# Revit family: IS_iLifeB_T5344_BIM_GB
name_source: partatom
category: Plumbing Fixtures
units: mm (PartAtom-declared; Revit-internal decimal feet)

## family parameters
Always vertical = No
Cut with Voids When Loaded = No
OmniClass Number = 23.45.05.14.14
OmniClass Title = Sinks/Lavatories
Part Type = Normal
Room Calculation Point = No
Round Connector Dimension = Use Diameter
Shared = No
Work Plane-Based = No

## types (2) — shared parameters
BIMobject category = Wash Basins
BIMobject category code = wash-basins
BIMobject main category = Sanitary
BIMobject main category code = sanitary
Brand url = http://www.idealstandard.co.uk
Date of publishing = 22/07/2022
Edition number = 1
GTIN code = https://8014140503873
IFC Classification = Sanitary Terminal
Installation instructions = https://www.idealstandard.co.uk
Manufacturer = Ideal Standard
Manufacturer name = Ideal Standard
Material main = Fireclay
NBS Reference Code = 45-35-70/368
NBS Reference Description = Wall hung hand rinse basins
NominalDepth = 440 mm
NominalHeight = 180 mm
NominalWidth = 549 mm
OmniClass Code = 23-39 29 13 21 19
OmniClass Description = Surface Water Retention Basins
Product Guid = 4836061b-5428-4228-a0b7-367d902eb1b3
Product SKU = T5344
Product certification = https://www.idealstandard.co.uk
Product data url = https://bimobject.com
Product family = Washbasin
Product group = Sanitary
Product name = I.Life b basin 55 cm with center taphole
Product url = https://www.idealstandard.co.uk
QR code = http://bimobject.com
Size = 550 x 440 x 180 mm
Technical description = https://www.idealstandard.co.uk
UNSPSC Code = 301815
URL = https://www.idealstandard.co.uk
Uniclass 2015 Code = Pr_40_20_96_96
Uniclass 2015 Name = Wall-hung washbasins
Youtube clip = https://www.youtube.com

## per-type parameters (varying)
| type | Description | Model |
| T534401 - Ideal Standard i.life B  basin 55 cm with center taphole and without overflow - White Finish | Ideal Standard i.life B  basin 55 cm with center taphole, without overflow, white, in carton box, EU pallet | T534401 |
| T5344MA - Ideal Standard i.life B  basin 55 cm with center taphole and without overflow  - Ideal Plus White | Ideal Standard i.life B  basin 55 cm with center taphole, without overflow, white Ideal Plus, in carton box, EU pallet | T5344MA |

## geometry (parser evidence)
native form markers: Sweep x3
no freeform markers — native parametric forms only
